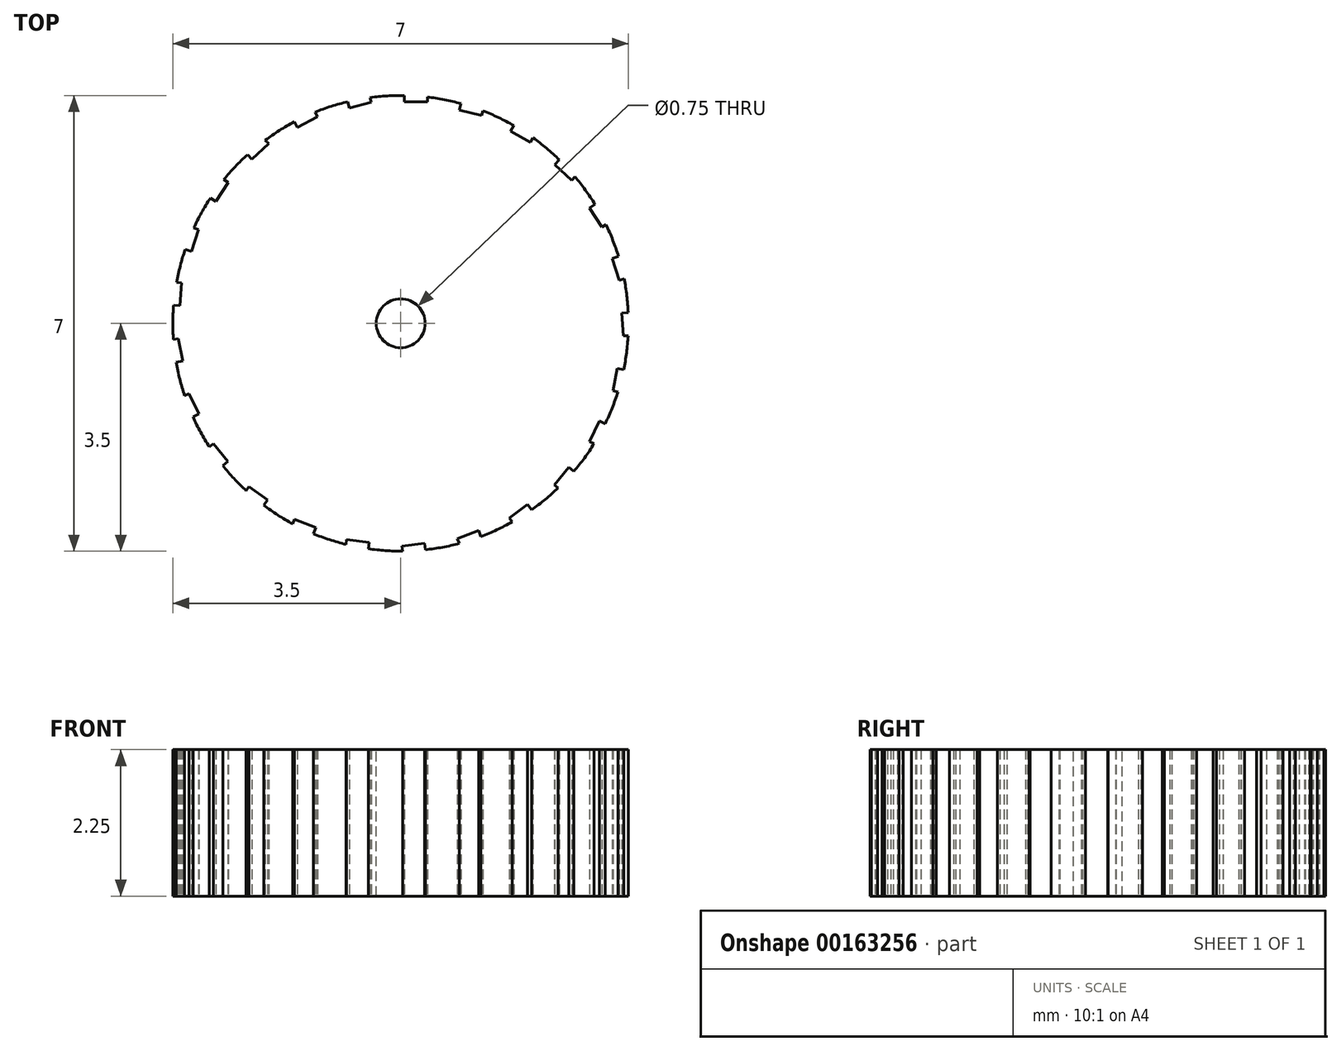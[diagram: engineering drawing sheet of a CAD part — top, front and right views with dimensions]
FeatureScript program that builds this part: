
annotation { "Feature Type Name" : "Feature", "Feature Type Description" : "" }
export const myFeature = defineFeature(function(context is Context, id is Id, definition is map)
    precondition{}
    {
        {
            var Q0;
            Q0=qCreatedBy(makeId("Top.planeOp"),FACE);
            var sketch = newSketch(context, id + "F0", { "sketchPlane" : qUnion([Q0])});
            skCircle(sketch, "E0", {"center": v(0, 0) * mm, "radius": 3.5 * mm});
            skLineSegment(sketch, "E1", {"start": v(0.06, 3.5) * mm, "end": v(0.06, 3.4) * mm});
            skLineSegment(sketch, "E2", {"start": v(0.06, 3.4) * mm, "end": v(0.4, 3.4) * mm});
            skLineSegment(sketch, "E3", {"start": v(0.4, 3.4) * mm, "end": v(0.4, 3.48) * mm});
            skArc(sketch, "E4", {"start": v(0.06, 3.5) * mm, "mid": v(0.23, 3.5) * mm, "end": v(0.4, 3.48) * mm});
            skLineSegment(sketch, "E5.1.0", {"start": v(-0.79, 3.3) * mm, "end": v(-0.45, 3.4) * mm});
            skLineSegment(sketch, "E5.1.1", {"start": v(-0.81, 3.4) * mm, "end": v(-0.79, 3.3) * mm});
            skArc(sketch, "E5.1.2", {"start": v(-0.81, 3.4) * mm, "mid": v(-0.64, 3.44) * mm, "end": v(-0.47, 3.47) * mm});
            skLineSegment(sketch, "E5.1.3", {"start": v(-0.45, 3.4) * mm, "end": v(-0.47, 3.47) * mm});
            skLineSegment(sketch, "E5.2.0", {"start": v(-1.59, 3) * mm, "end": v(-1.28, 3.18) * mm});
            skLineSegment(sketch, "E5.2.1", {"start": v(-1.63, 3.1) * mm, "end": v(-1.59, 3) * mm});
            skArc(sketch, "E5.2.2", {"start": v(-1.63, 3.1) * mm, "mid": v(-1.48, 3.17) * mm, "end": v(-1.32, 3.24) * mm});
            skLineSegment(sketch, "E5.2.3", {"start": v(-1.28, 3.18) * mm, "end": v(-1.32, 3.24) * mm});
            skLineSegment(sketch, "E5.3.0", {"start": v(-2.28, 2.52) * mm, "end": v(-2.03, 2.76) * mm});
            skLineSegment(sketch, "E5.3.1", {"start": v(-2.35, 2.6) * mm, "end": v(-2.28, 2.52) * mm});
            skArc(sketch, "E5.3.2", {"start": v(-2.35, 2.6) * mm, "mid": v(-2.22, 2.7) * mm, "end": v(-2.08, 2.81) * mm});
            skLineSegment(sketch, "E5.3.3", {"start": v(-2.03, 2.76) * mm, "end": v(-2.08, 2.81) * mm});
            skLineSegment(sketch, "E5.4.0", {"start": v(-2.84, 1.87) * mm, "end": v(-2.65, 2.17) * mm});
            skLineSegment(sketch, "E5.4.1", {"start": v(-2.92, 1.92) * mm, "end": v(-2.84, 1.87) * mm});
            skArc(sketch, "E5.4.2", {"start": v(-2.92, 1.92) * mm, "mid": v(-2.82, 2.07) * mm, "end": v(-2.72, 2.2) * mm});
            skLineSegment(sketch, "E5.4.3", {"start": v(-2.65, 2.17) * mm, "end": v(-2.72, 2.2) * mm});
            skLineSegment(sketch, "E5.5.0", {"start": v(-3.22, 1.1) * mm, "end": v(-3.1, 1.44) * mm});
            skLineSegment(sketch, "E5.5.1", {"start": v(-3.31, 1.14) * mm, "end": v(-3.22, 1.1) * mm});
            skArc(sketch, "E5.5.2", {"start": v(-3.31, 1.14) * mm, "mid": v(-3.25, 1.3) * mm, "end": v(-3.18, 1.46) * mm});
            skLineSegment(sketch, "E5.5.3", {"start": v(-3.1, 1.44) * mm, "end": v(-3.18, 1.46) * mm});
            skLineSegment(sketch, "E5.6.0", {"start": v(-3.39, 0.27) * mm, "end": v(-3.37, 0.62) * mm});
            skLineSegment(sketch, "E5.6.1", {"start": v(-3.49, 0.28) * mm, "end": v(-3.39, 0.27) * mm});
            skArc(sketch, "E5.6.2", {"start": v(-3.49, 0.28) * mm, "mid": v(-3.47, 0.45) * mm, "end": v(-3.44, 0.63) * mm});
            skLineSegment(sketch, "E5.6.3", {"start": v(-3.37, 0.62) * mm, "end": v(-3.44, 0.63) * mm});
            skLineSegment(sketch, "E5.7.0", {"start": v(-3.35, -0.58) * mm, "end": v(-3.42, -0.24) * mm});
            skLineSegment(sketch, "E5.7.1", {"start": v(-3.45, -0.6) * mm, "end": v(-3.35, -0.58) * mm});
            skArc(sketch, "E5.7.2", {"start": v(-3.45, -0.6) * mm, "mid": v(-3.47, -0.42) * mm, "end": v(-3.5, -0.25) * mm});
            skLineSegment(sketch, "E5.7.3", {"start": v(-3.42, -0.24) * mm, "end": v(-3.5, -0.25) * mm});
            skLineSegment(sketch, "E5.8.0", {"start": v(-3.1, -1.4) * mm, "end": v(-3.25, -1.08) * mm});
            skLineSegment(sketch, "E5.8.1", {"start": v(-3.2, -1.44) * mm, "end": v(-3.1, -1.4) * mm});
            skArc(sketch, "E5.8.2", {"start": v(-3.2, -1.44) * mm, "mid": v(-3.26, -1.28) * mm, "end": v(-3.32, -1.11) * mm});
            skLineSegment(sketch, "E5.8.3", {"start": v(-3.25, -1.08) * mm, "end": v(-3.32, -1.11) * mm});
            skLineSegment(sketch, "E5.9.0", {"start": v(-2.66, -2.12) * mm, "end": v(-2.88, -1.85) * mm});
            skLineSegment(sketch, "E5.9.1", {"start": v(-2.73, -2.19) * mm, "end": v(-2.66, -2.12) * mm});
            skArc(sketch, "E5.9.2", {"start": v(-2.73, -2.19) * mm, "mid": v(-2.84, -2.05) * mm, "end": v(-2.94, -1.9) * mm});
            skLineSegment(sketch, "E5.9.3", {"start": v(-2.88, -1.85) * mm, "end": v(-2.94, -1.9) * mm});
            skLineSegment(sketch, "E6.1.10.0", {"start": v(-2.05, -2.72) * mm, "end": v(-2.33, -2.51) * mm});
            skLineSegment(sketch, "E6.3.10.0", {"start": v(-2.1, -2.8) * mm, "end": v(-2.05, -2.72) * mm});
            skArc(sketch, "E6.6.10.0", {"start": v(-2.1, -2.8) * mm, "mid": v(-2.24, -2.69) * mm, "end": v(-2.37, -2.57) * mm});
            skLineSegment(sketch, "E6.10.10.0", {"start": v(-2.33, -2.51) * mm, "end": v(-2.37, -2.57) * mm});
            skLineSegment(sketch, "E6.1.11.0", {"start": v(-1.3, -3.14) * mm, "end": v(-1.63, -3.01) * mm});
            skLineSegment(sketch, "E6.3.11.0", {"start": v(-1.34, -3.23) * mm, "end": v(-1.3, -3.14) * mm});
            skArc(sketch, "E6.6.11.0", {"start": v(-1.34, -3.23) * mm, "mid": v(-1.5, -3.16) * mm, "end": v(-1.66, -3.08) * mm});
            skLineSegment(sketch, "E6.10.11.0", {"start": v(-1.63, -3.01) * mm, "end": v(-1.66, -3.08) * mm});
            skLineSegment(sketch, "E6.1.12.0", {"start": v(-0.48, -3.37) * mm, "end": v(-0.83, -3.32) * mm});
            skLineSegment(sketch, "E6.3.12.0", {"start": v(-0.5, -3.46) * mm, "end": v(-0.48, -3.37) * mm});
            skArc(sketch, "E6.6.12.0", {"start": v(-0.5, -3.46) * mm, "mid": v(-0.67, -3.44) * mm, "end": v(-0.84, -3.4) * mm});
            skLineSegment(sketch, "E6.10.12.0", {"start": v(-0.83, -3.32) * mm, "end": v(-0.84, -3.4) * mm});
            skLineSegment(sketch, "E6.1.13.0", {"start": v(0.37, -3.38) * mm, "end": v(0.02, -3.42) * mm});
            skLineSegment(sketch, "E6.3.13.0", {"start": v(0.38, -3.48) * mm, "end": v(0.37, -3.38) * mm});
            skArc(sketch, "E6.6.13.0", {"start": v(0.38, -3.48) * mm, "mid": v(0.2, -3.5) * mm, "end": v(0.03, -3.5) * mm});
            skLineSegment(sketch, "E6.10.13.0", {"start": v(0.02, -3.42) * mm, "end": v(0.03, -3.5) * mm});
            skLineSegment(sketch, "E7.1.14.0", {"start": v(1.2, -3.18) * mm, "end": v(0.87, -3.31) * mm});
            skLineSegment(sketch, "E7.3.14.0", {"start": v(1.23, -3.28) * mm, "end": v(1.2, -3.18) * mm});
            skArc(sketch, "E7.6.14.0", {"start": v(1.23, -3.28) * mm, "mid": v(1.07, -3.33) * mm, "end": v(0.9, -3.38) * mm});
            skLineSegment(sketch, "E7.10.14.0", {"start": v(0.87, -3.31) * mm, "end": v(0.9, -3.38) * mm});
            skLineSegment(sketch, "E7.1.15.0", {"start": v(1.95, -2.78) * mm, "end": v(1.67, -3) * mm});
            skLineSegment(sketch, "E7.3.15.0", {"start": v(2, -2.87) * mm, "end": v(1.95, -2.78) * mm});
            skArc(sketch, "E7.6.15.0", {"start": v(2, -2.87) * mm, "mid": v(1.86, -2.96) * mm, "end": v(1.71, -3.05) * mm});
            skLineSegment(sketch, "E7.10.15.0", {"start": v(1.67, -3) * mm, "end": v(1.71, -3.05) * mm});
            skLineSegment(sketch, "E7.1.16.0", {"start": v(2.58, -2.21) * mm, "end": v(2.36, -2.48) * mm});
            skLineSegment(sketch, "E7.3.16.0", {"start": v(2.66, -2.28) * mm, "end": v(2.58, -2.21) * mm});
            skArc(sketch, "E7.6.16.0", {"start": v(2.66, -2.28) * mm, "mid": v(2.54, -2.4) * mm, "end": v(2.42, -2.53) * mm});
            skLineSegment(sketch, "E7.10.16.0", {"start": v(2.36, -2.48) * mm, "end": v(2.42, -2.53) * mm});
            skLineSegment(sketch, "E7.1.17.0", {"start": v(3.05, -1.5) * mm, "end": v(2.9, -1.82) * mm});
            skLineSegment(sketch, "E7.3.17.0", {"start": v(3.14, -1.54) * mm, "end": v(3.05, -1.5) * mm});
            skArc(sketch, "E7.6.17.0", {"start": v(3.14, -1.54) * mm, "mid": v(3.06, -1.7) * mm, "end": v(2.97, -1.85) * mm});
            skLineSegment(sketch, "E7.10.17.0", {"start": v(2.9, -1.82) * mm, "end": v(2.97, -1.85) * mm});
            skLineSegment(sketch, "E7.1.18.0", {"start": v(3.33, -0.7) * mm, "end": v(3.26, -1.04) * mm});
            skLineSegment(sketch, "E7.3.18.0", {"start": v(3.43, -0.71) * mm, "end": v(3.33, -0.7) * mm});
            skArc(sketch, "E7.6.18.0", {"start": v(3.43, -0.71) * mm, "mid": v(3.39, -0.88) * mm, "end": v(3.34, -1.05) * mm});
            skLineSegment(sketch, "E7.10.18.0", {"start": v(3.26, -1.04) * mm, "end": v(3.34, -1.05) * mm});
            skLineSegment(sketch, "E7.1.19.0", {"start": v(3.4, 0.15) * mm, "end": v(3.42, -0.2) * mm});
            skLineSegment(sketch, "E7.3.19.0", {"start": v(3.5, 0.16) * mm, "end": v(3.4, 0.15) * mm});
            skArc(sketch, "E7.6.19.0", {"start": v(3.5, 0.16) * mm, "mid": v(3.5, -0.01) * mm, "end": v(3.5, -0.19) * mm});
            skLineSegment(sketch, "E7.10.19.0", {"start": v(3.42, -0.2) * mm, "end": v(3.5, -0.19) * mm});
            skLineSegment(sketch, "E8.1.20.0", {"start": v(3.25, 1) * mm, "end": v(3.36, 0.66) * mm});
            skLineSegment(sketch, "E8.3.20.0", {"start": v(3.35, 1.03) * mm, "end": v(3.25, 1) * mm});
            skArc(sketch, "E8.6.20.0", {"start": v(3.35, 1.03) * mm, "mid": v(3.4, 0.86) * mm, "end": v(3.43, 0.69) * mm});
            skLineSegment(sketch, "E8.10.20.0", {"start": v(3.36, 0.66) * mm, "end": v(3.43, 0.69) * mm});
            skLineSegment(sketch, "E8.1.21.0", {"start": v(2.9, 1.77) * mm, "end": v(3.09, 1.48) * mm});
            skLineSegment(sketch, "E8.3.21.0", {"start": v(2.99, 1.83) * mm, "end": v(2.9, 1.77) * mm});
            skArc(sketch, "E8.6.21.0", {"start": v(2.99, 1.83) * mm, "mid": v(3.07, 1.67) * mm, "end": v(3.15, 1.52) * mm});
            skLineSegment(sketch, "E8.10.21.0", {"start": v(3.09, 1.48) * mm, "end": v(3.15, 1.52) * mm});
            skLineSegment(sketch, "E8.1.22.0", {"start": v(2.37, 2.44) * mm, "end": v(2.62, 2.2) * mm});
            skLineSegment(sketch, "E8.3.22.0", {"start": v(2.44, 2.51) * mm, "end": v(2.37, 2.44) * mm});
            skArc(sketch, "E8.6.22.0", {"start": v(2.44, 2.51) * mm, "mid": v(2.56, 2.39) * mm, "end": v(2.68, 2.25) * mm});
            skLineSegment(sketch, "E8.10.22.0", {"start": v(2.62, 2.2) * mm, "end": v(2.68, 2.25) * mm});
            skLineSegment(sketch, "E8.1.23.0", {"start": v(1.69, 2.95) * mm, "end": v(2, 2.78) * mm});
            skLineSegment(sketch, "E8.3.23.0", {"start": v(1.74, 3.04) * mm, "end": v(1.69, 2.95) * mm});
            skArc(sketch, "E8.6.23.0", {"start": v(1.74, 3.04) * mm, "mid": v(1.89, 2.95) * mm, "end": v(2.03, 2.85) * mm});
            skLineSegment(sketch, "E8.10.23.0", {"start": v(2, 2.78) * mm, "end": v(2.03, 2.85) * mm});
            skLineSegment(sketch, "E8.1.24.0", {"start": v(0.9, 3.28) * mm, "end": v(1.24, 3.2) * mm});
            skLineSegment(sketch, "E8.3.24.0", {"start": v(0.93, 3.37) * mm, "end": v(0.9, 3.28) * mm});
            skArc(sketch, "E8.6.24.0", {"start": v(0.93, 3.37) * mm, "mid": v(1.1, 3.32) * mm, "end": v(1.26, 3.27) * mm});
            skLineSegment(sketch, "E8.10.24.0", {"start": v(1.24, 3.2) * mm, "end": v(1.26, 3.27) * mm});
            skSolve(sketch);
        }
        {
            var Q0;
            {var subQ24=sQuery(id+"F0.wireOp",EDGE,"E1");Q0=makeQuery(id+"F0.imprint","IMPRINT",FACE,{"disambiguationData":[TD([[makeQuery(id+"F0.imprint","IMPRINT",EDGE,{"derivedFrom":subQ24}),-1.0]])]});}
            extrude(context, id + "F1", {"entities" : qUnion([Q0]), "depth" : 2.25 * mm});
        }
        {
            var Q0;
            Q0=makeQuery(id+"F1.opExtrude","CAP_FACE",FACE,{"disambiguationData":[OSD([sQuery(id+"F0.wireOp",EDGE,"E0"),sQuery(id+"F0.wireOp",EDGE,"E1"),sQuery(id+"F0.wireOp",EDGE,"E2"),sQuery(id+"F0.wireOp",EDGE,"E3"),sQuery(id+"F0.wireOp",EDGE,"E5.1.0"),sQuery(id+"F0.wireOp",EDGE,"E5.1.1"),sQuery(id+"F0.wireOp",EDGE,"E5.1.3"),sQuery(id+"F0.wireOp",EDGE,"E5.2.0"),sQuery(id+"F0.wireOp",EDGE,"E5.2.1"),sQuery(id+"F0.wireOp",EDGE,"E5.2.3"),sQuery(id+"F0.wireOp",EDGE,"E5.3.0"),sQuery(id+"F0.wireOp",EDGE,"E5.3.1"),sQuery(id+"F0.wireOp",EDGE,"E5.3.3"),sQuery(id+"F0.wireOp",EDGE,"E5.4.0"),sQuery(id+"F0.wireOp",EDGE,"E5.4.1"),sQuery(id+"F0.wireOp",EDGE,"E5.4.3"),sQuery(id+"F0.wireOp",EDGE,"E5.5.0"),sQuery(id+"F0.wireOp",EDGE,"E5.5.1"),sQuery(id+"F0.wireOp",EDGE,"E5.5.3"),sQuery(id+"F0.wireOp",EDGE,"E5.6.0"),sQuery(id+"F0.wireOp",EDGE,"E5.6.1"),sQuery(id+"F0.wireOp",EDGE,"E5.6.3"),sQuery(id+"F0.wireOp",EDGE,"E5.7.0"),sQuery(id+"F0.wireOp",EDGE,"E5.7.1"),sQuery(id+"F0.wireOp",EDGE,"E5.7.3"),sQuery(id+"F0.wireOp",EDGE,"E5.8.0"),sQuery(id+"F0.wireOp",EDGE,"E5.8.1"),sQuery(id+"F0.wireOp",EDGE,"E5.8.3"),sQuery(id+"F0.wireOp",EDGE,"E5.9.0"),sQuery(id+"F0.wireOp",EDGE,"E5.9.1"),sQuery(id+"F0.wireOp",EDGE,"E5.9.3"),sQuery(id+"F0.wireOp",EDGE,"E6.1.10.0"),sQuery(id+"F0.wireOp",EDGE,"E6.3.10.0"),sQuery(id+"F0.wireOp",EDGE,"E6.10.10.0"),sQuery(id+"F0.wireOp",EDGE,"E6.1.11.0"),sQuery(id+"F0.wireOp",EDGE,"E6.3.11.0"),sQuery(id+"F0.wireOp",EDGE,"E6.10.11.0"),sQuery(id+"F0.wireOp",EDGE,"E6.1.12.0"),sQuery(id+"F0.wireOp",EDGE,"E6.3.12.0"),sQuery(id+"F0.wireOp",EDGE,"E6.10.12.0"),sQuery(id+"F0.wireOp",EDGE,"E6.1.13.0"),sQuery(id+"F0.wireOp",EDGE,"E6.3.13.0"),sQuery(id+"F0.wireOp",EDGE,"E6.10.13.0")])],"isStart":false});
            var sketch = newSketch(context, id + "F2", { "sketchPlane" : qUnion([Q0])});
            skCircle(sketch, "E9", {"center": v(0, 0) * mm, "radius": 0.37 * mm});
            skSolve(sketch);
        }
        {
            var Q0;
            Q0 = qSketchRegion(id + "F2", true);
            extrude(context, id + "F3", {"entities" : qUnion([Q0]), "operationType" : NewBodyOperationType.REMOVE, "endBound" : BoundingType.THROUGH_ALL, "oppositeDirection" : true, "depth" : 25 * mm});
        }
    });
